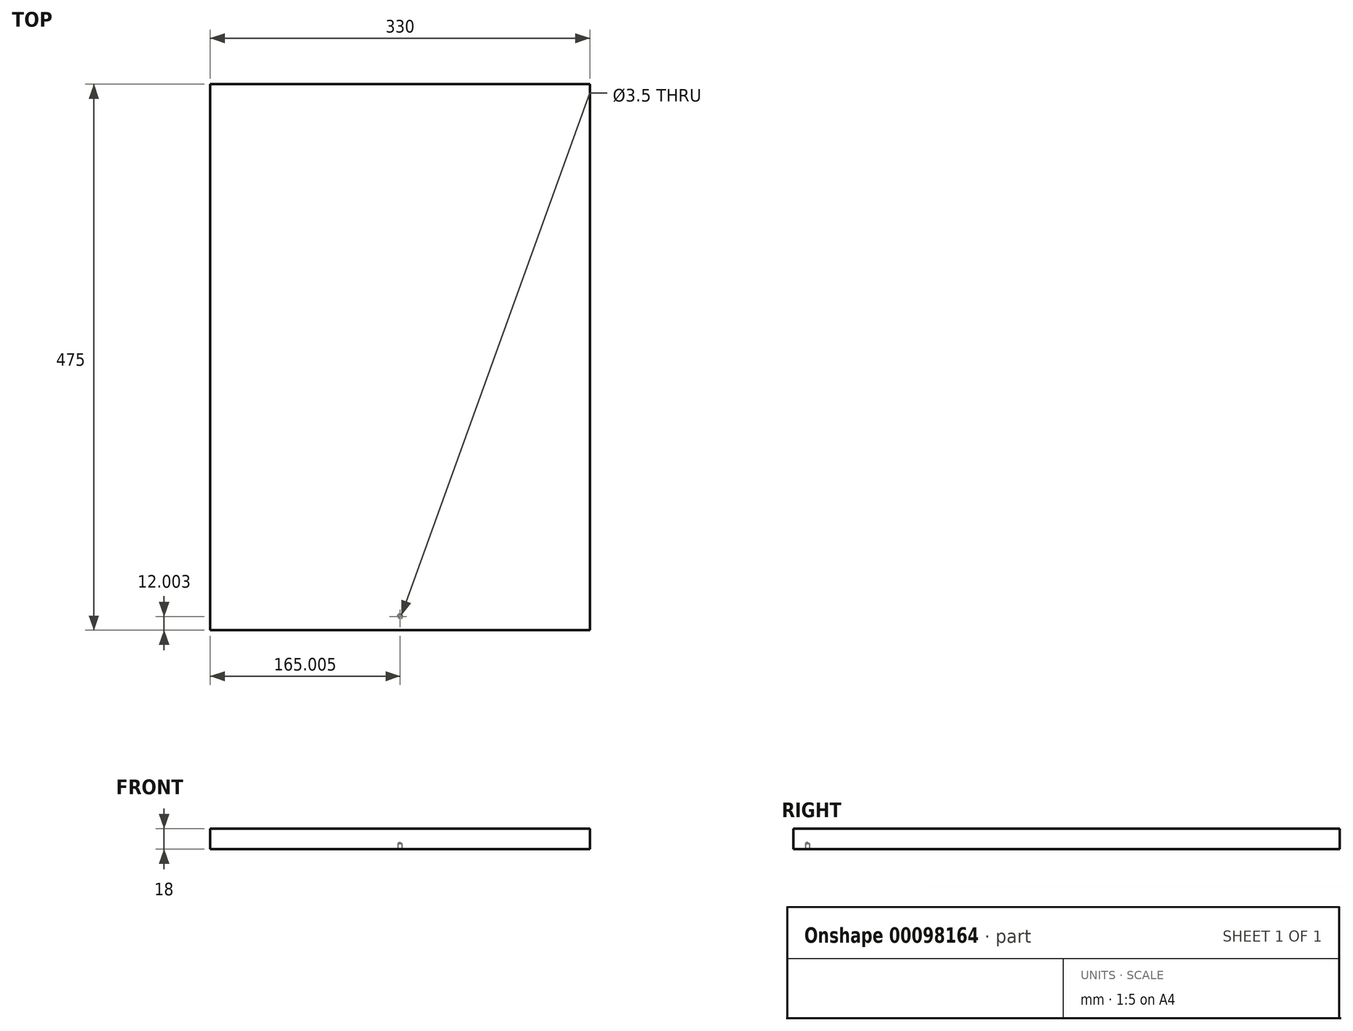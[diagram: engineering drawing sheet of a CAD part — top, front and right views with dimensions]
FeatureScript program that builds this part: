
annotation { "Feature Type Name" : "Feature", "Feature Type Description" : "" }
export const myFeature = defineFeature(function(context is Context, id is Id, definition is map)
    precondition{}
    {
        {
            var Q0;
            Q0=qCreatedBy(makeId("Top.planeOp"),FACE);
            var sketch = newSketch(context, id + "F0", { "sketchPlane" : qUnion([Q0])});
            skLineSegment(sketch, "E0.bottom", {"start": v(-499.57, 75.68) * mm, "end": v(-169.57, 75.68) * mm});
            skLineSegment(sketch, "E0.top", {"start": v(-499.57, -399.32) * mm, "end": v(-169.57, -399.32) * mm});
            skLineSegment(sketch, "E0.left", {"start": v(-499.57, 75.68) * mm, "end": v(-499.57, -399.32) * mm});
            skLineSegment(sketch, "E0.right", {"start": v(-169.57, 75.68) * mm, "end": v(-169.57, -399.32) * mm});
            skSolve(sketch);
        }
        {
            var Q0;
            Q0=makeQuery(id+"F0.imprint","IMPRINT",FACE,{"disambiguationData":[TD([[makeQuery(id+"F0.imprint","IMPRINT",EDGE,{"derivedFrom":sQuery(id+"F0.wireOp",EDGE,"E0.bottom")}),-1.0]])]});
            extrude(context, id + "F1", {"entities" : qUnion([Q0]), "depth" : 18 * mm});
        }
        {
            var Q0;
            Q0=makeQuery(id+"F1.opExtrude","CAP_FACE",FACE,{"disambiguationData":[OSD([sQuery(id+"F0.wireOp",EDGE,"E0.bottom"),sQuery(id+"F0.wireOp",EDGE,"E0.top"),sQuery(id+"F0.wireOp",EDGE,"E0.left"),sQuery(id+"F0.wireOp",EDGE,"E0.right")])],"isStart":true});
            var sketch = newSketch(context, id + "F2", { "sketchPlane" : qUnion([Q0])});
            skPoint(sketch, "E1", {"position": v(-334.57, 387.32) * mm});
            skSolve(sketch);
        }
        {
            var Q0;
            Q0=sQuery(id+"F2.wireOp",VERTEX,"E1");
            var Q1;
            Q1=sQuery(id+"F2.wireOp",VERTEX,"E1");
            var Q2;
            Q2=makeQuery(id+"F1.opExtrude","SWEPT_BODY",BODY,{"disambiguationData":[OSD([sQuery(id+"F0.wireOp",EDGE,"E0.bottom"),sQuery(id+"F0.wireOp",EDGE,"E0.top"),sQuery(id+"F0.wireOp",EDGE,"E0.left"),sQuery(id+"F0.wireOp",EDGE,"E0.right")])]});
            hole(context, id + "F3", {"style" : HoleStyle.C_SINK, "endStyle" : HoleEndStyle.BLIND, "holeDiameter" : 3.5 * mm, "cSinkDiameter" : 4.5 * mm, "cSinkAngle" : 90 * degree, "holeDepth" : 5 * mm, "locations" : qUnion([Q0, Q1]), "scope" : qUnion([Q2])});
        }
    });
